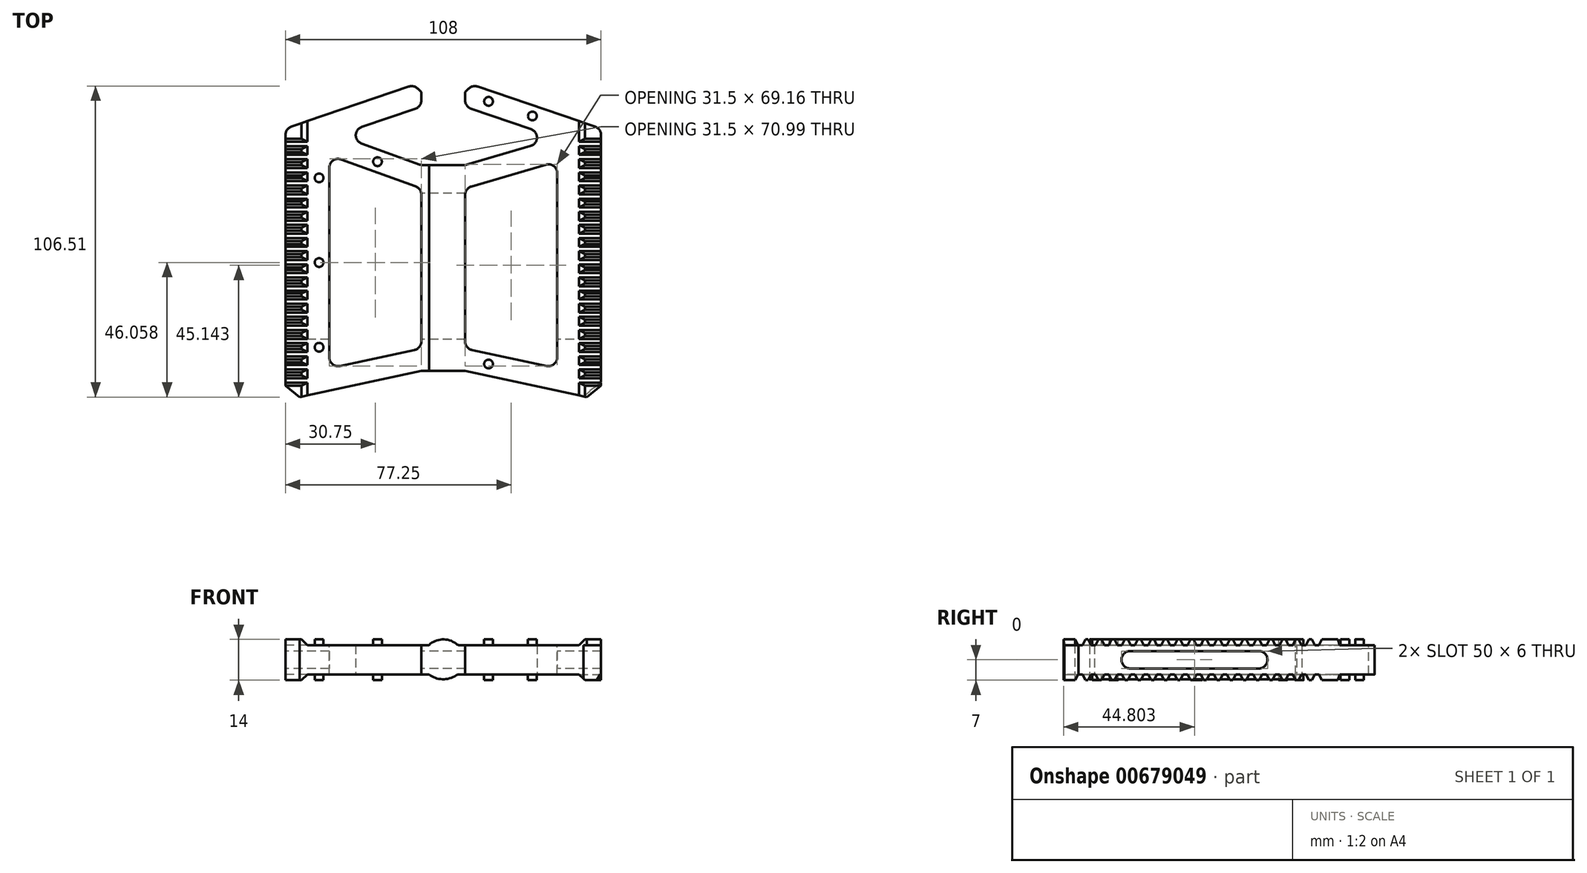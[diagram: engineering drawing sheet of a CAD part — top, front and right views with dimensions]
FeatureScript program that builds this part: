
annotation { "Feature Type Name" : "Feature", "Feature Type Description" : "" }
export const myFeature = defineFeature(function(context is Context, id is Id, definition is map)
    precondition{}
    {
        {
            var Q0;
            Q0=qCreatedBy(makeId("Top.planeOp"),FACE);
            var sketch = newSketch(context, id + "F0", { "sketchPlane" : qUnion([Q0])});
            skLineSegment(sketch, "E0.top", {"start": v(44, 108) * mm, "end": v(64, 108) * mm});
            skLineSegment(sketch, "E0.left", {"start": v(0, 0) * mm, "end": v(0, 93) * mm});
            skLineSegment(sketch, "E0.right", {"start": v(108, 0) * mm, "end": v(108, 93) * mm});
            skLineSegment(sketch, "E1", {"start": v(0, 0) * mm, "end": v(46.5, 10) * mm});
            skLineSegment(sketch, "E2", {"start": v(46.5, 10) * mm, "end": v(61.5, 10) * mm});
            skLineSegment(sketch, "E3", {"start": v(61.5, 10) * mm, "end": v(108, 0) * mm});
            skLineSegment(sketch, "E4", {"start": v(0, 93) * mm, "end": v(44, 108) * mm});
            skLineSegment(sketch, "E5", {"start": v(64, 108) * mm, "end": v(108, 93) * mm});
            skPoint(sketch, "E6.orphan", {"position": v(0, 108) * mm});
            skSolve(sketch);
        }
        {
            var Q0;
            Q0=qSketchRegion(id+"F0",true);
            extrude(context, id + "F1", {"entities" : qUnion([Q0]), "depth" : 10 * mm, "offsetDistance" : 25 * mm});
        }
        {
            var Q0;
            Q0=makeQuery(id+"F1.opExtrude","CAP_FACE",FACE,{"disambiguationData":[OSD([sQuery(id+"F0.wireOp",EDGE,"E0.top"),sQuery(id+"F0.wireOp",EDGE,"E0.left"),sQuery(id+"F0.wireOp",EDGE,"E0.right"),sQuery(id+"F0.wireOp",EDGE,"E1"),sQuery(id+"F0.wireOp",EDGE,"E2"),sQuery(id+"F0.wireOp",EDGE,"E3"),sQuery(id+"F0.wireOp",EDGE,"E4"),sQuery(id+"F0.wireOp",EDGE,"E5")])],"isStart":false});
            var sketch = newSketch(context, id + "F2", { "sketchPlane" : qUnion([Q0])});
            skLineSegment(sketch, "E7", {"start": v(18, 90.78) * mm, "end": v(46.5, 100.5) * mm});
            skLineSegment(sketch, "E8", {"start": v(61.5, 100.5) * mm, "end": v(93, 89.76) * mm});
            skLineSegment(sketch, "E9", {"start": v(93, 89.76) * mm, "end": v(61.5, 80.5) * mm});
            skLineSegment(sketch, "E10", {"start": v(61.5, 80.5) * mm, "end": v(46.5, 80.5) * mm});
            skLineSegment(sketch, "E11", {"start": v(46.5, 80.5) * mm, "end": v(18, 90.78) * mm});
            skLineSegment(sketch, "E12", {"start": v(15, 83.9) * mm, "end": v(46.5, 72.53) * mm});
            skLineSegment(sketch, "E13", {"start": v(46.5, 72.53) * mm, "end": v(46.5, 17.67) * mm});
            skLineSegment(sketch, "E14", {"start": v(46.5, 17.67) * mm, "end": v(15, 10.9) * mm});
            skLineSegment(sketch, "E15", {"start": v(15, 10.9) * mm, "end": v(15, 83.9) * mm});
            skLineSegment(sketch, "E16", {"start": v(61.5, 72.53) * mm, "end": v(93, 81.79) * mm});
            skLineSegment(sketch, "E17", {"start": v(93, 81.79) * mm, "end": v(93, 10.9) * mm});
            skLineSegment(sketch, "E18", {"start": v(93, 10.9) * mm, "end": v(61.5, 17.67) * mm});
            skLineSegment(sketch, "E19", {"start": v(61.5, 17.67) * mm, "end": v(61.5, 72.53) * mm});
            skLineSegment(sketch, "E20", {"start": v(44, 108) * mm, "end": v(46.5, 105.5) * mm});
            skLineSegment(sketch, "E21", {"start": v(61.5, 105.5) * mm, "end": v(64, 108) * mm});
            skLineSegment(sketch, "E22", {"start": v(46.5, 105.5) * mm, "end": v(46.5, 100.5) * mm});
            skLineSegment(sketch, "E23", {"start": v(61.5, 105.5) * mm, "end": v(61.5, 100.5) * mm});
            skSolve(sketch);
        }
        {
            var Q0;
            Q0=makeQuery(id+"F2.imprint","IMPRINT",FACE,{"disambiguationData":[TD([[makeQuery(id+"F2.imprint","IMPRINT",EDGE,{"derivedFrom":sQuery(id+"F2.wireOp",EDGE,"E12")}),-1.0]])]});
            var Q1;
            Q1=makeQuery(id+"F2.imprint","IMPRINT",FACE,{"disambiguationData":[TD([[makeQuery(id+"F2.imprint","IMPRINT",EDGE,{"derivedFrom":sQuery(id+"F2.wireOp",EDGE,"E16")}),-1.0]])]});
            var Q2;
            Q2=makeQuery(id+"F2.imprint","IMPRINT",FACE,{"disambiguationData":[TD([[makeQuery(id+"F2.imprint","IMPRINT",EDGE,{"derivedFrom":sQuery(id+"F2.wireOp",EDGE,"E7")}),-1.0]])]});
            var Q3;
            Q3=makeQuery(id+"F2.imprint","IMPRINT",FACE,{"disambiguationData":[TD([[makeQuery(id+"F2.imprint","IMPRINT",EDGE,{"derivedFrom":sQuery(id+"F2.wireOp",EDGE,"E20")}),1.0]])]});
            extrude(context, id + "F3", {"entities" : qUnion([Q0, Q1, Q2, Q3]), "operationType" : NewBodyOperationType.REMOVE, "oppositeDirection" : true, "depth" : 25 * mm, "offsetDistance" : 25 * mm});
        }
        {
            var Q0;
            Q0=makeQuery(id+"F1.opExtrude","SWEPT_EDGE",EDGE,{"disambiguationData":[OSD([sQuery(id+"F0.wireOp",EDGE,"E0.left"),sQuery(id+"F0.wireOp",EDGE,"E1")])]});
            var Q1;
            Q1=makeQuery(id+"F1.opExtrude","SWEPT_EDGE",EDGE,{"disambiguationData":[OSD([sQuery(id+"F0.wireOp",EDGE,"E0.right"),sQuery(id+"F0.wireOp",EDGE,"E3")])]});
            chamfer(context, id + "F4", {"entities" : qUnion([Q0, Q1]), "width" : 5 * mm, "tangentPropagation" : true});
        }
        {
            var Q0;
            Q0=makeQuery(id+"F3.boolean.opBoolean","COPY",EDGE,{"derivedFrom":makeQuery(id+"F3.opExtrude","SWEPT_EDGE",EDGE,{"disambiguationData":[OSD([sQuery(id+"F2.wireOp",EDGE,"E13"),sQuery(id+"F2.wireOp",EDGE,"E14")])]})});
            var Q1;
            Q1=makeQuery(id+"F3.boolean.opBoolean","COPY",EDGE,{"derivedFrom":makeQuery(id+"F3.opExtrude","SWEPT_EDGE",EDGE,{"disambiguationData":[OSD([sQuery(id+"F2.wireOp",EDGE,"E17"),sQuery(id+"F2.wireOp",EDGE,"E18")])]})});
            var Q2;
            Q2=makeQuery(id+"F3.boolean.opBoolean","COPY",EDGE,{"derivedFrom":makeQuery(id+"F3.opExtrude","SWEPT_EDGE",EDGE,{"disambiguationData":[OSD([sQuery(id+"F2.wireOp",EDGE,"E10"),sQuery(id+"F2.wireOp",EDGE,"E11")])]})});
            var Q3;
            Q3=makeQuery(id+"F3.boolean.opBoolean","COPY",EDGE,{"derivedFrom":makeQuery(id+"F3.opExtrude","SWEPT_EDGE",EDGE,{"disambiguationData":[OSD([sQuery(id+"F2.wireOp",EDGE,"E9"),sQuery(id+"F2.wireOp",EDGE,"E10")])]})});
            var Q4;
            Q4=makeQuery(id+"F3.boolean.opBoolean","COPY",EDGE,{"derivedFrom":makeQuery(id+"F3.opExtrude","SWEPT_EDGE",EDGE,{"disambiguationData":[OSD([sQuery(id+"F2.wireOp",EDGE,"E18"),sQuery(id+"F2.wireOp",EDGE,"E19")])]})});
            var Q5;
            Q5=makeQuery(id+"F3.boolean.opBoolean","COPY",EDGE,{"derivedFrom":makeQuery(id+"F3.opExtrude","SWEPT_EDGE",EDGE,{"disambiguationData":[OSD([sQuery(id+"F2.wireOp",EDGE,"E14"),sQuery(id+"F2.wireOp",EDGE,"E15")])]})});
            var Q6;
            Q6=makeQuery(id+"F3.boolean.opBoolean","COPY",EDGE,{"derivedFrom":makeQuery(id+"F3.opExtrude","SWEPT_EDGE",EDGE,{"disambiguationData":[OSD([sQuery(id+"F2.wireOp",EDGE,"E16"),sQuery(id+"F2.wireOp",EDGE,"E17")])]})});
            var Q7;
            Q7=makeQuery(id+"F3.boolean.opBoolean","COPY",EDGE,{"derivedFrom":makeQuery(id+"F3.opExtrude","SWEPT_EDGE",EDGE,{"disambiguationData":[OSD([sQuery(id+"F2.wireOp",EDGE,"E12"),sQuery(id+"F2.wireOp",EDGE,"E13")])]})});
            var Q8;
            Q8=makeQuery(id+"F3.boolean.opBoolean","COPY",EDGE,{"derivedFrom":makeQuery(id+"F3.opExtrude","SWEPT_EDGE",EDGE,{"disambiguationData":[OSD([sQuery(id+"F2.wireOp",EDGE,"E12"),sQuery(id+"F2.wireOp",EDGE,"E15")])]})});
            var Q9;
            Q9=makeQuery(id+"F3.boolean.opBoolean","COPY",EDGE,{"derivedFrom":makeQuery(id+"F3.opExtrude","SWEPT_EDGE",EDGE,{"disambiguationData":[OSD([sQuery(id+"F2.wireOp",EDGE,"E7"),sQuery(id+"F2.wireOp",EDGE,"HO8CVhf7-1jhG-dmqV-wMaq-zJcC65SmTLqd")])]})});
            var Q10;
            Q10=makeQuery(id+"F3.boolean.opBoolean","COPY",EDGE,{"derivedFrom":makeQuery(id+"F3.opExtrude","SWEPT_EDGE",EDGE,{"disambiguationData":[OSD([sQuery(id+"F2.wireOp",EDGE,"HO8CVhf7-1jhG-dmqV-wMaq-zJcC65SmTLqd"),sQuery(id+"F2.wireOp",EDGE,"E8")])]})});
            var Q11;
            Q11=makeQuery(id+"F3.boolean.opBoolean","COPY",EDGE,{"derivedFrom":makeQuery(id+"F3.opExtrude","SWEPT_EDGE",EDGE,{"disambiguationData":[OSD([sQuery(id+"F2.wireOp",EDGE,"E8"),sQuery(id+"F2.wireOp",EDGE,"E9")])]})});
            var Q12;
            Q12=makeQuery(id+"F3.boolean.opBoolean","COPY",EDGE,{"derivedFrom":makeQuery(id+"F3.opExtrude","SWEPT_EDGE",EDGE,{"disambiguationData":[OSD([sQuery(id+"F2.wireOp",EDGE,"E7"),sQuery(id+"F2.wireOp",EDGE,"E11")])]})});
            var Q13;
            Q13=makeQuery(id+"F3.boolean.opBoolean","COPY",EDGE,{"derivedFrom":makeQuery(id+"F3.opExtrude","SWEPT_EDGE",EDGE,{"disambiguationData":[OSD([sQuery(id+"F2.wireOp",EDGE,"E16"),sQuery(id+"F2.wireOp",EDGE,"E19")])]})});
            var Q14;
            Q14=makeQuery(id+"F1.opExtrude","SWEPT_EDGE",EDGE,{"disambiguationData":[OSD([sQuery(id+"F0.wireOp",EDGE,"E0.right"),sQuery(id+"F0.wireOp",EDGE,"E5")])]});
            var Q15;
            Q15=makeQuery(id+"F1.opExtrude","SWEPT_EDGE",EDGE,{"disambiguationData":[OSD([sQuery(id+"F0.wireOp",EDGE,"E0.left"),sQuery(id+"F0.wireOp",EDGE,"E4")])]});
            var Q16;
            {var subQ0=sQuery(id+"F0.wireOp",EDGE,"E5");var subQ1=sQuery(id+"F0.wireOp",EDGE,"E0.top");Q16=makeQuery(id+"F3.boolean.opBoolean","MERGE",EDGE,{"derivedFrom":[makeQuery(id+"F1.opExtrude","SWEPT_EDGE",EDGE,{"disambiguationData":[OSD([subQ1,subQ0])]}),makeQuery(id+"F3.opExtrude","SWEPT_EDGE",EDGE,{"disambiguationData":[OSD([subQ1,subQ0,sQuery(id+"F2.wireOp",EDGE,"E21")])]})]});}
            var Q17;
            {var subQ0=sQuery(id+"F0.wireOp",EDGE,"E4");var subQ1=sQuery(id+"F0.wireOp",EDGE,"E0.top");Q17=makeQuery(id+"F3.boolean.opBoolean","MERGE",EDGE,{"derivedFrom":[makeQuery(id+"F1.opExtrude","SWEPT_EDGE",EDGE,{"disambiguationData":[OSD([subQ1,subQ0])]}),makeQuery(id+"F3.opExtrude","SWEPT_EDGE",EDGE,{"disambiguationData":[OSD([subQ1,subQ0,sQuery(id+"F2.wireOp",EDGE,"E20")])]})]});}
            fillet(context, id + "F5", {"entities" : qUnion([Q0, Q1, Q2, Q3, Q4, Q5, Q6, Q7, Q8, Q9, Q10, Q11, Q12, Q13, Q14, Q15, Q16, Q17]), "radius" : 3 * mm, "tangentPropagation" : true, "allowEdgeOverflow" : false});
        }
        {
            var Q0;
            Q0=makeQuery(id+"F1.opExtrude","CAP_FACE",FACE,{"disambiguationData":[OSD([sQuery(id+"F0.wireOp",EDGE,"E0.top"),sQuery(id+"F0.wireOp",EDGE,"E0.left"),sQuery(id+"F0.wireOp",EDGE,"E0.right"),sQuery(id+"F0.wireOp",EDGE,"E1"),sQuery(id+"F0.wireOp",EDGE,"E2"),sQuery(id+"F0.wireOp",EDGE,"E3"),sQuery(id+"F0.wireOp",EDGE,"E4"),sQuery(id+"F0.wireOp",EDGE,"E5")])],"isStart":false});
            var sketch = newSketch(context, id + "F6", { "sketchPlane" : qUnion([Q0])});
            skLineSegment(sketch, "E24", {"start": v(100.5, 95.56) * mm, "end": v(100.5, 1.61) * mm});
            skLineSegment(sketch, "E25", {"start": v(103.11, 1.05) * mm, "end": v(108, 5) * mm});
            skLineSegment(sketch, "E26", {"start": v(108, 5) * mm, "end": v(108, 90.85) * mm});
            skLineSegment(sketch, "E27", {"start": v(100.5, 95.56) * mm, "end": v(105.97, 93.7) * mm});
            skArc(sketch, "E28", {"start": v(108, 90.85) * mm, "mid": v(107.44, 92.6) * mm, "end": v(105.97, 93.7) * mm});
            skLineSegment(sketch, "E29", {"start": v(103.11, 1.05) * mm, "end": v(100.5, 1.61) * mm});
            skSolve(sketch);
        }
        {
            var Q0;
            {var subQ2=sQuery(id+"F6.wireOp",EDGE,"E24");Q0=makeQuery(id+"F6.imprint","IMPRINT",FACE,{"disambiguationData":[TD([[makeQuery(id+"F6.imprint","IMPRINT",EDGE,{"derivedFrom":subQ2}),1.0]])]});}
            extrude(context, id + "F7", {"entities" : qUnion([Q0]), "operationType" : NewBodyOperationType.ADD, "depth" : 2 * mm, "offsetDistance" : 25 * mm, "hasSecondDirection" : true, "secondDirectionOppositeDirection" : true, "secondDirectionDepth" : 12 * mm});
        }
        {
            var Q0;
            Q0=qSketchRegion(id+"F6",true);
            extrude(context, id + "F8", {"entities" : qUnion([Q0]), "operationType" : NewBodyOperationType.ADD, "depth" : 2 * mm, "offsetDistance" : 25 * mm});
        }
        {
            var Q0;
            Q0=makeQuery(id+"F1.opExtrude","CAP_FACE",FACE,{"disambiguationData":[OSD([sQuery(id+"F0.wireOp",EDGE,"E0.top"),sQuery(id+"F0.wireOp",EDGE,"E0.left"),sQuery(id+"F0.wireOp",EDGE,"E0.right"),sQuery(id+"F0.wireOp",EDGE,"E1"),sQuery(id+"F0.wireOp",EDGE,"E2"),sQuery(id+"F0.wireOp",EDGE,"E3"),sQuery(id+"F0.wireOp",EDGE,"E4"),sQuery(id+"F0.wireOp",EDGE,"E5")])],"isStart":true});
            var sketch = newSketch(context, id + "F9", { "sketchPlane" : qUnion([Q0])});
            skLineSegment(sketch, "E30", {"start": v(7.5, -95.56) * mm, "end": v(7.5, -1.61) * mm});
            skLineSegment(sketch, "E31", {"start": v(7.5, -1.61) * mm, "end": v(4.89, -1.05) * mm});
            skLineSegment(sketch, "E32", {"start": v(4.89, -1.05) * mm, "end": v(0, -5) * mm});
            skLineSegment(sketch, "E33", {"start": v(0, -5) * mm, "end": v(0, -90.85) * mm});
            skLineSegment(sketch, "E34", {"start": v(2.03, -93.7) * mm, "end": v(7.5, -95.56) * mm});
            skArc(sketch, "E35", {"start": v(0, -90.85) * mm, "mid": v(0.56, -92.6) * mm, "end": v(2.03, -93.7) * mm});
            skSolve(sketch);
        }
        {
            var Q0;
            Q0=qSketchRegion(id+"F9",true);
            extrude(context, id + "F10", {"entities" : qUnion([Q0]), "operationType" : NewBodyOperationType.ADD, "depth" : 2 * mm, "offsetDistance" : 25 * mm, "hasSecondDirection" : true, "secondDirectionOppositeDirection" : true, "secondDirectionDepth" : 12 * mm});
        }
        {
            var Q0;
            Q0=makeQuery(id+"F7.opExtrude","CAP_EDGE",EDGE,{"disambiguationData":[OSD([sQuery(id+"F6.wireOp",EDGE,"E24")])],"isStart":false});
            var Q1;
            Q1=makeQuery(id+"F10.opExtrude","CAP_EDGE",EDGE,{"disambiguationData":[OSD([sQuery(id+"F9.wireOp",EDGE,"E30")])],"isStart":false});
            var Q2;
            Q2=makeQuery(id+"F7.opExtrude","CAP_EDGE",EDGE,{"disambiguationData":[OSD([sQuery(id+"F6.wireOp",EDGE,"E24")])],"isStart":true});
            var Q3;
            Q3=makeQuery(id+"F10.opExtrude","CAP_EDGE",EDGE,{"disambiguationData":[OSD([sQuery(id+"F9.wireOp",EDGE,"E30")])],"isStart":true});
            chamfer(context, id + "F11", {"entities" : qUnion([Q0, Q1, Q2, Q3]), "width" : 2 * mm, "tangentPropagation" : true});
        }
        {
            var Q0;
            Q0=makeQuery(id+"F1.opExtrude","CAP_FACE",FACE,{"disambiguationData":[OSD([sQuery(id+"F0.wireOp",EDGE,"E0.top"),sQuery(id+"F0.wireOp",EDGE,"E0.left"),sQuery(id+"F0.wireOp",EDGE,"E0.right"),sQuery(id+"F0.wireOp",EDGE,"E1"),sQuery(id+"F0.wireOp",EDGE,"E2"),sQuery(id+"F0.wireOp",EDGE,"E3"),sQuery(id+"F0.wireOp",EDGE,"E4"),sQuery(id+"F0.wireOp",EDGE,"E5")])],"isStart":false});
            var sketch = newSketch(context, id + "F12", { "sketchPlane" : qUnion([Q0])});
            skCircle(sketch, "E36", {"center": v(69.5, 102.34) * mm, "radius": 1.5 * mm});
            skCircle(sketch, "E37", {"center": v(84.5, 97.31) * mm, "radius": 1.5 * mm});
            skCircle(sketch, "E38", {"center": v(69.5, 12.37) * mm, "radius": 1.5 * mm});
            skCircle(sketch, "E39", {"center": v(11.5, 76.12) * mm, "radius": 1.5 * mm});
            skCircle(sketch, "E40", {"center": v(11.5, 47.12) * mm, "radius": 1.5 * mm});
            skCircle(sketch, "E41", {"center": v(11.5, 18.11) * mm, "radius": 1.5 * mm});
            skCircle(sketch, "E42", {"center": v(31.5, 81.66) * mm, "radius": 1.5 * mm});
            skSolve(sketch);
        }
        {
            var Q0;
            Q0=qSketchRegion(id+"F12",true);
            extrude(context, id + "F13", {"entities" : qUnion([Q0]), "operationType" : NewBodyOperationType.ADD, "depth" : 2 * mm, "offsetDistance" : 25 * mm, "hasSecondDirection" : true, "secondDirectionOppositeDirection" : true, "secondDirectionDepth" : 12 * mm});
        }
        {
            var Q0;
            Q0=makeQuery(id+"F1.opExtrude","SWEPT_FACE",FACE,{"disambiguationData":[OSD([sQuery(id+"F0.wireOp",EDGE,"E2")])]});
            var sketch = newSketch(context, id + "F14", { "sketchPlane" : qUnion([Q0])});
            skArc(sketch, "E43", {"start": v(58.9, 10) * mm, "mid": v(54, 12) * mm, "end": v(49.1, 10) * mm});
            skArc(sketch, "E44", {"start": v(49.1, 0) * mm, "mid": v(54, -1.68) * mm, "end": v(58.9, 0) * mm});
            skLineSegment(sketch, "E45", {"start": v(49.1, 10) * mm, "end": v(58.9, 10) * mm});
            skLineSegment(sketch, "E46", {"start": v(58.9, 0) * mm, "end": v(49.1, 0) * mm});
            skSolve(sketch);
        }
        {
            var Q0;
            Q0=makeQuery(id+"F14.imprint","IMPRINT",FACE,{"disambiguationData":[TD([[makeQuery(id+"F14.imprint","IMPRINT",EDGE,{"derivedFrom":sQuery(id+"F14.wireOp",EDGE,"E43")}),1.0]])]});
            var Q1;
            Q1=makeQuery(id+"F14.imprint","IMPRINT",FACE,{"disambiguationData":[TD([[makeQuery(id+"F14.imprint","IMPRINT",EDGE,{"derivedFrom":sQuery(id+"F14.wireOp",EDGE,"E44")}),1.0]])]});
            var Q2;
            Q2=makeQuery(id+"F3.boolean.opBoolean","COPY",FACE,{"derivedFrom":makeQuery(id+"F3.opExtrude","SWEPT_FACE",FACE,{"disambiguationData":[OSD([sQuery(id+"F2.wireOp",EDGE,"E10")])]})});
            extrude(context, id + "F15", {"entities" : qUnion([Q0, Q1]), "operationType" : NewBodyOperationType.ADD, "endBound" : BoundingType.UP_TO_SURFACE, "oppositeDirection" : true, "depth" : 25 * mm, "endBoundEntityFace" : qUnion([Q2]), "offsetDistance" : 25 * mm});
        }
        {
            var Q0;
            {var subQ0=sQuery(id+"F14.wireOp",EDGE,"E46");var subQ1=sQuery(id+"F14.wireOp",EDGE,"E44");var subQ2=sQuery(id+"F0.wireOp",EDGE,"E2");Q0=makeQuery(id+"F15.opExtrude","SWEPT_EDGE",EDGE,{"disambiguationData":[OSD([subQ2,subQ1,subQ0]),TDD([makeQuery(id+"F14.imprint","INTERSECT",VERTEX,{"disambiguationData":[OD(0.0)],"derivedFrom":[makeQuery(id+"F1.opExtrude","CAP_EDGE",EDGE,{"disambiguationData":[OSD([subQ2])],"isStart":true}),subQ1,subQ0]})])]});}
            var Q1;
            {var subQ0=sQuery(id+"F14.wireOp",EDGE,"E46");var subQ1=sQuery(id+"F14.wireOp",EDGE,"E44");var subQ2=sQuery(id+"F0.wireOp",EDGE,"E2");Q1=makeQuery(id+"F15.opExtrude","SWEPT_EDGE",EDGE,{"disambiguationData":[OSD([subQ2,subQ1,subQ0]),TDD([makeQuery(id+"F14.imprint","INTERSECT",VERTEX,{"disambiguationData":[OD(1.0)],"derivedFrom":[makeQuery(id+"F1.opExtrude","CAP_EDGE",EDGE,{"disambiguationData":[OSD([subQ2])],"isStart":true}),subQ1,subQ0]})])]});}
            var Q2;
            {var subQ0=sQuery(id+"F14.wireOp",EDGE,"E45");var subQ1=sQuery(id+"F14.wireOp",EDGE,"E43");var subQ2=sQuery(id+"F0.wireOp",EDGE,"E2");Q2=makeQuery(id+"F15.opExtrude","SWEPT_EDGE",EDGE,{"disambiguationData":[OSD([subQ2,subQ1,subQ0]),TDD([makeQuery(id+"F14.imprint","INTERSECT",VERTEX,{"disambiguationData":[OD(1.0)],"derivedFrom":[makeQuery(id+"F1.opExtrude","CAP_EDGE",EDGE,{"disambiguationData":[OSD([subQ2])],"isStart":false}),subQ1,subQ0]})])]});}
            var Q3;
            {var subQ0=sQuery(id+"F14.wireOp",EDGE,"E45");var subQ1=sQuery(id+"F14.wireOp",EDGE,"E43");var subQ2=sQuery(id+"F0.wireOp",EDGE,"E2");Q3=makeQuery(id+"F15.opExtrude","SWEPT_EDGE",EDGE,{"disambiguationData":[OSD([subQ2,subQ1,subQ0]),TDD([makeQuery(id+"F14.imprint","INTERSECT",VERTEX,{"disambiguationData":[OD(0.0)],"derivedFrom":[makeQuery(id+"F1.opExtrude","CAP_EDGE",EDGE,{"disambiguationData":[OSD([subQ2])],"isStart":false}),subQ1,subQ0]})])]});}
            fillet(context, id + "F16", {"entities" : qUnion([Q0, Q1, Q2, Q3]), "radius" : 2 * mm, "tangentPropagation" : true, "allowEdgeOverflow" : false});
        }
        {
            var Q0;
            Q0=makeQuery(id+"F10.boolean.opBoolean","MERGE",FACE,{"derivedFrom":[makeQuery(id+"F1.opExtrude","SWEPT_FACE",FACE,{"disambiguationData":[OSD([sQuery(id+"F0.wireOp",EDGE,"E0.left")])]}),makeQuery(id+"F10.opExtrude","SWEPT_FACE",FACE,{"disambiguationData":[OSD([sQuery(id+"F9.wireOp",EDGE,"E33")])]})]});
            cPlane(context, id + "F17", {"entities" : qUnion([Q0]), "cplaneType" : CPlaneType.OFFSET, "offset" : 54 * mm, "oppositeDirection" : true, "width" : 150 * mm, "height" : 150 * mm});
        }
        {
            var Q0;
            Q0=qCreatedBy(id+"F17.planeOp",FACE);
            var sketch = newSketch(context, id + "F18", { "sketchPlane" : qUnion([Q0])});
            skLineSegment(sketch, "E47.bottom", {"start": v(-67.85, 8) * mm, "end": v(-23.85, 8) * mm});
            skLineSegment(sketch, "E47.top", {"start": v(-67.85, 2) * mm, "end": v(-23.85, 2) * mm});
            skLineSegment(sketch, "E47.left", {"start": v(-70.85, 5) * mm, "end": v(-70.85, 5) * mm});
            skLineSegment(sketch, "E47.right", {"start": v(-20.85, 5) * mm, "end": v(-20.85, 5) * mm});
            skPoint(sketch, "E48.visualSharp", {"position": v(-70.85, 8) * mm});
            skArc(sketch, "E48.filletArc", {"start": v(-67.85, 8) * mm, "mid": v(-69.97, 7.12) * mm, "end": v(-70.85, 5) * mm});
            skPoint(sketch, "E49.visualSharp", {"position": v(-70.85, 2) * mm});
            skArc(sketch, "E49.filletArc", {"start": v(-70.85, 5) * mm, "mid": v(-69.97, 2.88) * mm, "end": v(-67.85, 2) * mm});
            skPoint(sketch, "E50.visualSharp", {"position": v(-20.85, 2) * mm});
            skArc(sketch, "E50.filletArc", {"start": v(-23.85, 2) * mm, "mid": v(-21.73, 2.88) * mm, "end": v(-20.85, 5) * mm});
            skPoint(sketch, "E51.visualSharp", {"position": v(-20.85, 8) * mm});
            skArc(sketch, "E51.filletArc", {"start": v(-20.85, 5) * mm, "mid": v(-21.73, 7.12) * mm, "end": v(-23.85, 8) * mm});
            skSolve(sketch);
        }
        {
            var Q0;
            Q0 = qSketchRegion(id + "F18", true);
            extrude(context, id + "F19", {"entities" : qUnion([Q0]), "operationType" : NewBodyOperationType.REMOVE, "endBound" : BoundingType.THROUGH_ALL, "oppositeDirection" : true, "depth" : 25 * mm, "offsetDistance" : 25 * mm, "hasSecondDirection" : true, "secondDirectionBound" : SecondDirectionBoundingType.THROUGH_ALL, "secondDirectionOppositeDirection" : false, "secondDirectionDepth" : 25 * mm});
        }
        {
            var Q0;
            Q0=makeQuery(id+"F10.boolean.opBoolean","MERGE",FACE,{"derivedFrom":[makeQuery(id+"F1.opExtrude","SWEPT_FACE",FACE,{"disambiguationData":[OSD([sQuery(id+"F0.wireOp",EDGE,"E0.left")])]}),makeQuery(id+"F10.opExtrude","SWEPT_FACE",FACE,{"disambiguationData":[OSD([sQuery(id+"F9.wireOp",EDGE,"E33")])]})]});
            var sketch = newSketch(context, id + "F20", { "sketchPlane" : qUnion([Q0])});
            skLineSegment(sketch, "E52", {"start": v(-5, 12) * mm, "end": v(-6, 10) * mm});
            skLineSegment(sketch, "E53", {"start": v(-6, 10) * mm, "end": v(-7.5, 10) * mm});
            skLineSegment(sketch, "E54", {"start": v(-7.5, 10) * mm, "end": v(-8.5, 12) * mm});
            skLineSegment(sketch, "E55", {"start": v(-8.5, 12) * mm, "end": v(-5, 12) * mm});
            skLineSegment(sketch, "E56.1.0.0", {"start": v(-9.5, 12) * mm, "end": v(-10.5, 10) * mm});
            skLineSegment(sketch, "E56.1.0.1", {"start": v(-10.5, 10) * mm, "end": v(-12, 10) * mm});
            skLineSegment(sketch, "E56.1.0.2", {"start": v(-12, 10) * mm, "end": v(-13, 12) * mm});
            skLineSegment(sketch, "E56.1.0.3", {"start": v(-13, 12) * mm, "end": v(-9.5, 12) * mm});
            skLineSegment(sketch, "E56.2.0.0", {"start": v(-14, 12) * mm, "end": v(-15, 10) * mm});
            skLineSegment(sketch, "E56.2.0.1", {"start": v(-15, 10) * mm, "end": v(-16.5, 10) * mm});
            skLineSegment(sketch, "E56.2.0.2", {"start": v(-16.5, 10) * mm, "end": v(-17.5, 12) * mm});
            skLineSegment(sketch, "E56.2.0.3", {"start": v(-17.5, 12) * mm, "end": v(-14, 12) * mm});
            skLineSegment(sketch, "E56.3.0.0", {"start": v(-18.5, 12) * mm, "end": v(-19.5, 10) * mm});
            skLineSegment(sketch, "E56.3.0.1", {"start": v(-19.5, 10) * mm, "end": v(-21, 10) * mm});
            skLineSegment(sketch, "E56.3.0.2", {"start": v(-21, 10) * mm, "end": v(-22, 12) * mm});
            skLineSegment(sketch, "E56.3.0.3", {"start": v(-22, 12) * mm, "end": v(-18.5, 12) * mm});
            skLineSegment(sketch, "E56.4.0.0", {"start": v(-23, 12) * mm, "end": v(-24, 10) * mm});
            skLineSegment(sketch, "E56.4.0.1", {"start": v(-24, 10) * mm, "end": v(-25.5, 10) * mm});
            skLineSegment(sketch, "E56.4.0.2", {"start": v(-25.5, 10) * mm, "end": v(-26.5, 12) * mm});
            skLineSegment(sketch, "E56.4.0.3", {"start": v(-26.5, 12) * mm, "end": v(-23, 12) * mm});
            skLineSegment(sketch, "E56.5.0.0", {"start": v(-27.5, 12) * mm, "end": v(-28.5, 10) * mm});
            skLineSegment(sketch, "E56.5.0.1", {"start": v(-28.5, 10) * mm, "end": v(-30, 10) * mm});
            skLineSegment(sketch, "E56.5.0.2", {"start": v(-30, 10) * mm, "end": v(-31, 12) * mm});
            skLineSegment(sketch, "E56.5.0.3", {"start": v(-31, 12) * mm, "end": v(-27.5, 12) * mm});
            skLineSegment(sketch, "E56.6.0.0", {"start": v(-32, 12) * mm, "end": v(-33, 10) * mm});
            skLineSegment(sketch, "E56.6.0.1", {"start": v(-33, 10) * mm, "end": v(-34.5, 10) * mm});
            skLineSegment(sketch, "E56.6.0.2", {"start": v(-34.5, 10) * mm, "end": v(-35.5, 12) * mm});
            skLineSegment(sketch, "E56.6.0.3", {"start": v(-35.5, 12) * mm, "end": v(-32, 12) * mm});
            skLineSegment(sketch, "E56.7.0.0", {"start": v(-36.5, 12) * mm, "end": v(-37.5, 10) * mm});
            skLineSegment(sketch, "E56.7.0.1", {"start": v(-37.5, 10) * mm, "end": v(-39, 10) * mm});
            skLineSegment(sketch, "E56.7.0.2", {"start": v(-39, 10) * mm, "end": v(-40, 12) * mm});
            skLineSegment(sketch, "E56.7.0.3", {"start": v(-40, 12) * mm, "end": v(-36.5, 12) * mm});
            skLineSegment(sketch, "E56.8.0.0", {"start": v(-41, 12) * mm, "end": v(-42, 10) * mm});
            skLineSegment(sketch, "E56.8.0.1", {"start": v(-42, 10) * mm, "end": v(-43.5, 10) * mm});
            skLineSegment(sketch, "E56.8.0.2", {"start": v(-43.5, 10) * mm, "end": v(-44.5, 12) * mm});
            skLineSegment(sketch, "E56.8.0.3", {"start": v(-44.5, 12) * mm, "end": v(-41, 12) * mm});
            skLineSegment(sketch, "E56.9.0.0", {"start": v(-45.5, 12) * mm, "end": v(-46.5, 10) * mm});
            skLineSegment(sketch, "E56.9.0.1", {"start": v(-46.5, 10) * mm, "end": v(-48, 10) * mm});
            skLineSegment(sketch, "E56.9.0.2", {"start": v(-48, 10) * mm, "end": v(-49, 12) * mm});
            skLineSegment(sketch, "E56.9.0.3", {"start": v(-49, 12) * mm, "end": v(-45.5, 12) * mm});
            skLineSegment(sketch, "E56.10.0.0", {"start": v(-50, 12) * mm, "end": v(-51, 10) * mm});
            skLineSegment(sketch, "E56.10.0.1", {"start": v(-51, 10) * mm, "end": v(-52.5, 10) * mm});
            skLineSegment(sketch, "E56.10.0.2", {"start": v(-52.5, 10) * mm, "end": v(-53.5, 12) * mm});
            skLineSegment(sketch, "E56.10.0.3", {"start": v(-53.5, 12) * mm, "end": v(-50, 12) * mm});
            skLineSegment(sketch, "E56.11.0.0", {"start": v(-54.5, 12) * mm, "end": v(-55.5, 10) * mm});
            skLineSegment(sketch, "E56.11.0.1", {"start": v(-55.5, 10) * mm, "end": v(-57, 10) * mm});
            skLineSegment(sketch, "E56.11.0.2", {"start": v(-57, 10) * mm, "end": v(-58, 12) * mm});
            skLineSegment(sketch, "E56.11.0.3", {"start": v(-58, 12) * mm, "end": v(-54.5, 12) * mm});
            skLineSegment(sketch, "E56.12.0.0", {"start": v(-59, 12) * mm, "end": v(-60, 10) * mm});
            skLineSegment(sketch, "E56.12.0.1", {"start": v(-60, 10) * mm, "end": v(-61.5, 10) * mm});
            skLineSegment(sketch, "E56.12.0.2", {"start": v(-61.5, 10) * mm, "end": v(-62.5, 12) * mm});
            skLineSegment(sketch, "E56.12.0.3", {"start": v(-62.5, 12) * mm, "end": v(-59, 12) * mm});
            skLineSegment(sketch, "E56.13.0.0", {"start": v(-63.5, 12) * mm, "end": v(-64.5, 10) * mm});
            skLineSegment(sketch, "E56.13.0.1", {"start": v(-64.5, 10) * mm, "end": v(-66, 10) * mm});
            skLineSegment(sketch, "E56.13.0.2", {"start": v(-66, 10) * mm, "end": v(-67, 12) * mm});
            skLineSegment(sketch, "E56.13.0.3", {"start": v(-67, 12) * mm, "end": v(-63.5, 12) * mm});
            skLineSegment(sketch, "E56.14.0.0", {"start": v(-68, 12) * mm, "end": v(-69, 10) * mm});
            skLineSegment(sketch, "E56.14.0.1", {"start": v(-69, 10) * mm, "end": v(-70.5, 10) * mm});
            skLineSegment(sketch, "E56.14.0.2", {"start": v(-70.5, 10) * mm, "end": v(-71.5, 12) * mm});
            skLineSegment(sketch, "E56.14.0.3", {"start": v(-71.5, 12) * mm, "end": v(-68, 12) * mm});
            skLineSegment(sketch, "E56.15.0.0", {"start": v(-72.5, 12) * mm, "end": v(-73.5, 10) * mm});
            skLineSegment(sketch, "E56.15.0.1", {"start": v(-73.5, 10) * mm, "end": v(-75, 10) * mm});
            skLineSegment(sketch, "E56.15.0.2", {"start": v(-75, 10) * mm, "end": v(-76, 12) * mm});
            skLineSegment(sketch, "E56.15.0.3", {"start": v(-76, 12) * mm, "end": v(-72.5, 12) * mm});
            skLineSegment(sketch, "E56.16.0.0", {"start": v(-77, 12) * mm, "end": v(-78, 10) * mm});
            skLineSegment(sketch, "E56.16.0.1", {"start": v(-78, 10) * mm, "end": v(-79.5, 10) * mm});
            skLineSegment(sketch, "E56.16.0.2", {"start": v(-79.5, 10) * mm, "end": v(-80.5, 12) * mm});
            skLineSegment(sketch, "E56.16.0.3", {"start": v(-80.5, 12) * mm, "end": v(-77, 12) * mm});
            skLineSegment(sketch, "E56.17.0.0", {"start": v(-81.5, 12) * mm, "end": v(-82.5, 10) * mm});
            skLineSegment(sketch, "E56.17.0.1", {"start": v(-82.5, 10) * mm, "end": v(-84, 10) * mm});
            skLineSegment(sketch, "E56.17.0.2", {"start": v(-84, 10) * mm, "end": v(-85, 12) * mm});
            skLineSegment(sketch, "E56.17.0.3", {"start": v(-85, 12) * mm, "end": v(-81.5, 12) * mm});
            skLineSegment(sketch, "E56.18.0.0", {"start": v(-86, 12) * mm, "end": v(-87, 10) * mm});
            skLineSegment(sketch, "E56.18.0.1", {"start": v(-87, 10) * mm, "end": v(-88.5, 10) * mm});
            skLineSegment(sketch, "E56.18.0.2", {"start": v(-88.5, 10) * mm, "end": v(-89.5, 12) * mm});
            skLineSegment(sketch, "E56.18.0.3", {"start": v(-89.5, 12) * mm, "end": v(-86, 12) * mm});
            skLineSegment(sketch, "E56.direction1", {"start": v(-7.5, 10) * mm, "end": v(-12, 10) * mm, "construction": true});
            skLineSegment(sketch, "E57", {"start": v(1.3, 5) * mm, "end": v(-117.54, 5) * mm, "construction": true});
            skLineSegment(sketch, "E58.MirrorCS", {"start": v(-15, 0) * mm, "end": v(-16.5, 0) * mm});
            skLineSegment(sketch, "E59.MirrorCS", {"start": v(-12, 0) * mm, "end": v(-13, -2) * mm});
            skLineSegment(sketch, "E60.MirrorCS", {"start": v(-10.5, 0) * mm, "end": v(-12, 0) * mm});
            skLineSegment(sketch, "E61.MirrorCS", {"start": v(-9.5, -2) * mm, "end": v(-10.5, 0) * mm});
            skLineSegment(sketch, "E62.MirrorCS", {"start": v(-7.5, 0) * mm, "end": v(-8.5, -2) * mm});
            skLineSegment(sketch, "E63.MirrorCS", {"start": v(-6, 0) * mm, "end": v(-7.5, 0) * mm});
            skLineSegment(sketch, "E64.MirrorCS", {"start": v(-5, -2) * mm, "end": v(-6, 0) * mm});
            skLineSegment(sketch, "E65.MirrorCS", {"start": v(-21, 0) * mm, "end": v(-22, -2) * mm});
            skLineSegment(sketch, "E66.MirrorCS", {"start": v(-19.5, 0) * mm, "end": v(-21, 0) * mm});
            skLineSegment(sketch, "E67.MirrorCS", {"start": v(-48, 0) * mm, "end": v(-49, -2) * mm});
            skLineSegment(sketch, "E68.MirrorCS", {"start": v(-66, 0) * mm, "end": v(-67, -2) * mm});
            skLineSegment(sketch, "E69.MirrorCS", {"start": v(-84, 0) * mm, "end": v(-85, -2) * mm});
            skLineSegment(sketch, "E70.MirrorCS", {"start": v(-30, 0) * mm, "end": v(-31, -2) * mm});
            skLineSegment(sketch, "E71.MirrorCS", {"start": v(-7.5, 0) * mm, "end": v(-12, 0) * mm, "construction": true});
            skLineSegment(sketch, "E72.MirrorCS", {"start": v(-36.5, -2) * mm, "end": v(-37.5, 0) * mm});
            skLineSegment(sketch, "E73.MirrorCS", {"start": v(-54.5, -2) * mm, "end": v(-55.5, 0) * mm});
            skLineSegment(sketch, "E74.MirrorCS", {"start": v(-72.5, -2) * mm, "end": v(-73.5, 0) * mm});
            skLineSegment(sketch, "E75.MirrorCS", {"start": v(-39, 0) * mm, "end": v(-40, -2) * mm});
            skLineSegment(sketch, "E76.MirrorCS", {"start": v(-46.5, 0) * mm, "end": v(-48, 0) * mm});
            skLineSegment(sketch, "E77.MirrorCS", {"start": v(-57, 0) * mm, "end": v(-58, -2) * mm});
            skLineSegment(sketch, "E78.MirrorCS", {"start": v(-64.5, 0) * mm, "end": v(-66, 0) * mm});
            skLineSegment(sketch, "E79.MirrorCS", {"start": v(-82.5, 0) * mm, "end": v(-84, 0) * mm});
            skLineSegment(sketch, "E80.MirrorCS", {"start": v(-75, 0) * mm, "end": v(-76, -2) * mm});
            skLineSegment(sketch, "E81.MirrorCS", {"start": v(-28.5, 0) * mm, "end": v(-30, 0) * mm});
            skLineSegment(sketch, "E82.MirrorCS", {"start": v(-45.5, -2) * mm, "end": v(-46.5, 0) * mm});
            skLineSegment(sketch, "E83.MirrorCS", {"start": v(-37.5, 0) * mm, "end": v(-39, 0) * mm});
            skLineSegment(sketch, "E84.MirrorCS", {"start": v(-63.5, -2) * mm, "end": v(-64.5, 0) * mm});
            skLineSegment(sketch, "E85.MirrorCS", {"start": v(-55.5, 0) * mm, "end": v(-57, 0) * mm});
            skLineSegment(sketch, "E86.MirrorCS", {"start": v(-81.5, -2) * mm, "end": v(-82.5, 0) * mm});
            skLineSegment(sketch, "E87.MirrorCS", {"start": v(-73.5, 0) * mm, "end": v(-75, 0) * mm});
            skLineSegment(sketch, "E88.MirrorCS", {"start": v(-27.5, -2) * mm, "end": v(-28.5, 0) * mm});
            skLineSegment(sketch, "E89.MirrorCS", {"start": v(-88.5, 0) * mm, "end": v(-89.5, -2) * mm});
            skLineSegment(sketch, "E90.MirrorCS", {"start": v(-34.5, 0) * mm, "end": v(-35.5, -2) * mm});
            skLineSegment(sketch, "E91.MirrorCS", {"start": v(-52.5, 0) * mm, "end": v(-53.5, -2) * mm});
            skLineSegment(sketch, "E92.MirrorCS", {"start": v(-70.5, 0) * mm, "end": v(-71.5, -2) * mm});
            skLineSegment(sketch, "E93.MirrorCS", {"start": v(-33, 0) * mm, "end": v(-34.5, 0) * mm});
            skLineSegment(sketch, "E94.MirrorCS", {"start": v(-51, 0) * mm, "end": v(-52.5, 0) * mm});
            skLineSegment(sketch, "E95.MirrorCS", {"start": v(-69, 0) * mm, "end": v(-70.5, 0) * mm});
            skLineSegment(sketch, "E96.MirrorCS", {"start": v(-43.5, 0) * mm, "end": v(-44.5, -2) * mm});
            skLineSegment(sketch, "E97.MirrorCS", {"start": v(-61.5, 0) * mm, "end": v(-62.5, -2) * mm});
            skLineSegment(sketch, "E98.MirrorCS", {"start": v(-79.5, 0) * mm, "end": v(-80.5, -2) * mm});
            skLineSegment(sketch, "E99.MirrorCS", {"start": v(-87, 0) * mm, "end": v(-88.5, 0) * mm});
            skLineSegment(sketch, "E100.MirrorCS", {"start": v(-25.5, 0) * mm, "end": v(-26.5, -2) * mm});
            skLineSegment(sketch, "E101.MirrorCS", {"start": v(-42, 0) * mm, "end": v(-43.5, 0) * mm});
            skLineSegment(sketch, "E102.MirrorCS", {"start": v(-60, 0) * mm, "end": v(-61.5, 0) * mm});
            skLineSegment(sketch, "E103.MirrorCS", {"start": v(-59, -2) * mm, "end": v(-60, 0) * mm});
            skLineSegment(sketch, "E104.MirrorCS", {"start": v(-32, -2) * mm, "end": v(-33, 0) * mm});
            skLineSegment(sketch, "E105.MirrorCS", {"start": v(-24, 0) * mm, "end": v(-25.5, 0) * mm});
            skLineSegment(sketch, "E106.MirrorCS", {"start": v(-41, -2) * mm, "end": v(-42, 0) * mm});
            skLineSegment(sketch, "E107.MirrorCS", {"start": v(-68, -2) * mm, "end": v(-69, 0) * mm});
            skLineSegment(sketch, "E108.MirrorCS", {"start": v(-18.5, -2) * mm, "end": v(-19.5, 0) * mm});
            skLineSegment(sketch, "E109.MirrorCS", {"start": v(-14, -2) * mm, "end": v(-15, 0) * mm});
            skLineSegment(sketch, "E110.MirrorCS", {"start": v(-50, -2) * mm, "end": v(-51, 0) * mm});
            skLineSegment(sketch, "E111.MirrorCS", {"start": v(-86, -2) * mm, "end": v(-87, 0) * mm});
            skLineSegment(sketch, "E112.MirrorCS", {"start": v(-78, 0) * mm, "end": v(-79.5, 0) * mm});
            skLineSegment(sketch, "E113.MirrorCS", {"start": v(-23, -2) * mm, "end": v(-24, 0) * mm});
            skLineSegment(sketch, "E114.MirrorCS", {"start": v(-16.5, 0) * mm, "end": v(-17.5, -2) * mm});
            skLineSegment(sketch, "E115.MirrorCS", {"start": v(-77, -2) * mm, "end": v(-78, 0) * mm});
            skLineSegment(sketch, "E116.MirrorCS", {"start": v(-49, -2) * mm, "end": v(-45.5, -2) * mm});
            skLineSegment(sketch, "E117.MirrorCS", {"start": v(-31, -2) * mm, "end": v(-27.5, -2) * mm});
            skLineSegment(sketch, "E118.MirrorCS", {"start": v(-67, -2) * mm, "end": v(-63.5, -2) * mm});
            skLineSegment(sketch, "E119.MirrorCS", {"start": v(-13, -2) * mm, "end": v(-9.5, -2) * mm});
            skLineSegment(sketch, "E120.MirrorCS", {"start": v(-8.5, -2) * mm, "end": v(-5, -2) * mm});
            skLineSegment(sketch, "E121.MirrorCS", {"start": v(-22, -2) * mm, "end": v(-18.5, -2) * mm});
            skLineSegment(sketch, "E122.MirrorCS", {"start": v(-40, -2) * mm, "end": v(-36.5, -2) * mm});
            skLineSegment(sketch, "E123.MirrorCS", {"start": v(-58, -2) * mm, "end": v(-54.5, -2) * mm});
            skLineSegment(sketch, "E124.MirrorCS", {"start": v(-76, -2) * mm, "end": v(-72.5, -2) * mm});
            skLineSegment(sketch, "E125.MirrorCS", {"start": v(-89.5, -2) * mm, "end": v(-86, -2) * mm});
            skLineSegment(sketch, "E126.MirrorCS", {"start": v(-35.5, -2) * mm, "end": v(-32, -2) * mm});
            skLineSegment(sketch, "E127.MirrorCS", {"start": v(-53.5, -2) * mm, "end": v(-50, -2) * mm});
            skLineSegment(sketch, "E128.MirrorCS", {"start": v(-71.5, -2) * mm, "end": v(-68, -2) * mm});
            skLineSegment(sketch, "E129.MirrorCS", {"start": v(-44.5, -2) * mm, "end": v(-41, -2) * mm});
            skLineSegment(sketch, "E130.MirrorCS", {"start": v(-62.5, -2) * mm, "end": v(-59, -2) * mm});
            skLineSegment(sketch, "E131.MirrorCS", {"start": v(-80.5, -2) * mm, "end": v(-77, -2) * mm});
            skLineSegment(sketch, "E132.MirrorCS", {"start": v(-26.5, -2) * mm, "end": v(-23, -2) * mm});
            skLineSegment(sketch, "E133.MirrorCS", {"start": v(-17.5, -2) * mm, "end": v(-14, -2) * mm});
            skLineSegment(sketch, "E134.MirrorCS", {"start": v(-85, -2) * mm, "end": v(-81.5, -2) * mm});
            skSolve(sketch);
        }
        {
            var Q0;
            Q0=makeQuery(id+"F20.imprint","IMPRINT",FACE,{"disambiguationData":[TD([[makeQuery(id+"F20.imprint","IMPRINT",EDGE,{"derivedFrom":sQuery(id+"F20.wireOp",EDGE,"E56.18.0.0")}),-1.0]])]});
            var Q1;
            Q1=makeQuery(id+"F20.imprint","IMPRINT",FACE,{"disambiguationData":[TD([[makeQuery(id+"F20.imprint","IMPRINT",EDGE,{"derivedFrom":sQuery(id+"F20.wireOp",EDGE,"E56.17.0.0")}),-1.0]])]});
            var Q2;
            Q2=makeQuery(id+"F20.imprint","IMPRINT",FACE,{"disambiguationData":[TD([[makeQuery(id+"F20.imprint","IMPRINT",EDGE,{"derivedFrom":sQuery(id+"F20.wireOp",EDGE,"E56.16.0.0")}),-1.0]])]});
            var Q3;
            Q3=makeQuery(id+"F20.imprint","IMPRINT",FACE,{"disambiguationData":[TD([[makeQuery(id+"F20.imprint","IMPRINT",EDGE,{"derivedFrom":sQuery(id+"F20.wireOp",EDGE,"E56.15.0.0")}),-1.0]])]});
            var Q4;
            Q4=makeQuery(id+"F20.imprint","IMPRINT",FACE,{"disambiguationData":[TD([[makeQuery(id+"F20.imprint","IMPRINT",EDGE,{"derivedFrom":sQuery(id+"F20.wireOp",EDGE,"E56.14.0.0")}),-1.0]])]});
            var Q5;
            Q5=makeQuery(id+"F20.imprint","IMPRINT",FACE,{"disambiguationData":[TD([[makeQuery(id+"F20.imprint","IMPRINT",EDGE,{"derivedFrom":sQuery(id+"F20.wireOp",EDGE,"E56.13.0.0")}),-1.0]])]});
            var Q6;
            Q6=makeQuery(id+"F20.imprint","IMPRINT",FACE,{"disambiguationData":[TD([[makeQuery(id+"F20.imprint","IMPRINT",EDGE,{"derivedFrom":sQuery(id+"F20.wireOp",EDGE,"E56.12.0.0")}),-1.0]])]});
            var Q7;
            Q7=makeQuery(id+"F20.imprint","IMPRINT",FACE,{"disambiguationData":[TD([[makeQuery(id+"F20.imprint","IMPRINT",EDGE,{"derivedFrom":sQuery(id+"F20.wireOp",EDGE,"E56.11.0.0")}),-1.0]])]});
            var Q8;
            Q8=makeQuery(id+"F20.imprint","IMPRINT",FACE,{"disambiguationData":[TD([[makeQuery(id+"F20.imprint","IMPRINT",EDGE,{"derivedFrom":sQuery(id+"F20.wireOp",EDGE,"E56.10.0.0")}),-1.0]])]});
            var Q9;
            Q9=makeQuery(id+"F20.imprint","IMPRINT",FACE,{"disambiguationData":[TD([[makeQuery(id+"F20.imprint","IMPRINT",EDGE,{"derivedFrom":sQuery(id+"F20.wireOp",EDGE,"E56.9.0.0")}),-1.0]])]});
            var Q10;
            Q10=makeQuery(id+"F20.imprint","IMPRINT",FACE,{"disambiguationData":[TD([[makeQuery(id+"F20.imprint","IMPRINT",EDGE,{"derivedFrom":sQuery(id+"F20.wireOp",EDGE,"E56.8.0.0")}),-1.0]])]});
            var Q11;
            Q11=makeQuery(id+"F20.imprint","IMPRINT",FACE,{"disambiguationData":[TD([[makeQuery(id+"F20.imprint","IMPRINT",EDGE,{"derivedFrom":sQuery(id+"F20.wireOp",EDGE,"E56.7.0.0")}),-1.0]])]});
            var Q12;
            Q12=makeQuery(id+"F20.imprint","IMPRINT",FACE,{"disambiguationData":[TD([[makeQuery(id+"F20.imprint","IMPRINT",EDGE,{"derivedFrom":sQuery(id+"F20.wireOp",EDGE,"E56.6.0.0")}),-1.0]])]});
            var Q13;
            Q13=makeQuery(id+"F20.imprint","IMPRINT",FACE,{"disambiguationData":[TD([[makeQuery(id+"F20.imprint","IMPRINT",EDGE,{"derivedFrom":sQuery(id+"F20.wireOp",EDGE,"E56.5.0.0")}),-1.0]])]});
            var Q14;
            Q14=makeQuery(id+"F20.imprint","IMPRINT",FACE,{"disambiguationData":[TD([[makeQuery(id+"F20.imprint","IMPRINT",EDGE,{"derivedFrom":sQuery(id+"F20.wireOp",EDGE,"E56.4.0.0")}),-1.0]])]});
            var Q15;
            Q15=makeQuery(id+"F20.imprint","IMPRINT",FACE,{"disambiguationData":[TD([[makeQuery(id+"F20.imprint","IMPRINT",EDGE,{"derivedFrom":sQuery(id+"F20.wireOp",EDGE,"E56.3.0.0")}),-1.0]])]});
            var Q16;
            Q16=makeQuery(id+"F20.imprint","IMPRINT",FACE,{"disambiguationData":[TD([[makeQuery(id+"F20.imprint","IMPRINT",EDGE,{"derivedFrom":sQuery(id+"F20.wireOp",EDGE,"E56.2.0.0")}),-1.0]])]});
            var Q17;
            Q17=makeQuery(id+"F20.imprint","IMPRINT",FACE,{"disambiguationData":[TD([[makeQuery(id+"F20.imprint","IMPRINT",EDGE,{"derivedFrom":sQuery(id+"F20.wireOp",EDGE,"E56.1.0.0")}),-1.0]])]});
            var Q18;
            Q18=makeQuery(id+"F20.imprint","IMPRINT",FACE,{"disambiguationData":[TD([[makeQuery(id+"F20.imprint","IMPRINT",EDGE,{"derivedFrom":sQuery(id+"F20.wireOp",EDGE,"E52")}),-1.0]])]});
            var Q19;
            Q19=makeQuery(id+"F20.imprint","IMPRINT",FACE,{"disambiguationData":[TD([[makeQuery(id+"F20.imprint","IMPRINT",EDGE,{"derivedFrom":sQuery(id+"F20.wireOp",EDGE,"E89.MirrorCS")}),1.0]])]});
            var Q20;
            Q20=makeQuery(id+"F20.imprint","IMPRINT",FACE,{"disambiguationData":[TD([[makeQuery(id+"F20.imprint","IMPRINT",EDGE,{"derivedFrom":sQuery(id+"F20.wireOp",EDGE,"E69.MirrorCS")}),1.0]])]});
            var Q21;
            Q21=makeQuery(id+"F20.imprint","IMPRINT",FACE,{"disambiguationData":[TD([[makeQuery(id+"F20.imprint","IMPRINT",EDGE,{"derivedFrom":sQuery(id+"F20.wireOp",EDGE,"E98.MirrorCS")}),1.0]])]});
            var Q22;
            Q22=makeQuery(id+"F20.imprint","IMPRINT",FACE,{"disambiguationData":[TD([[makeQuery(id+"F20.imprint","IMPRINT",EDGE,{"derivedFrom":sQuery(id+"F20.wireOp",EDGE,"E74.MirrorCS")}),1.0]])]});
            var Q23;
            Q23=makeQuery(id+"F20.imprint","IMPRINT",FACE,{"disambiguationData":[TD([[makeQuery(id+"F20.imprint","IMPRINT",EDGE,{"derivedFrom":sQuery(id+"F20.wireOp",EDGE,"E92.MirrorCS")}),1.0]])]});
            var Q24;
            Q24=makeQuery(id+"F20.imprint","IMPRINT",FACE,{"disambiguationData":[TD([[makeQuery(id+"F20.imprint","IMPRINT",EDGE,{"derivedFrom":sQuery(id+"F20.wireOp",EDGE,"E68.MirrorCS")}),1.0]])]});
            var Q25;
            Q25=makeQuery(id+"F20.imprint","IMPRINT",FACE,{"disambiguationData":[TD([[makeQuery(id+"F20.imprint","IMPRINT",EDGE,{"derivedFrom":sQuery(id+"F20.wireOp",EDGE,"E97.MirrorCS")}),1.0]])]});
            var Q26;
            Q26=makeQuery(id+"F20.imprint","IMPRINT",FACE,{"disambiguationData":[TD([[makeQuery(id+"F20.imprint","IMPRINT",EDGE,{"derivedFrom":sQuery(id+"F20.wireOp",EDGE,"E73.MirrorCS")}),1.0]])]});
            var Q27;
            Q27=makeQuery(id+"F20.imprint","IMPRINT",FACE,{"disambiguationData":[TD([[makeQuery(id+"F20.imprint","IMPRINT",EDGE,{"derivedFrom":sQuery(id+"F20.wireOp",EDGE,"E91.MirrorCS")}),1.0]])]});
            var Q28;
            Q28=makeQuery(id+"F20.imprint","IMPRINT",FACE,{"disambiguationData":[TD([[makeQuery(id+"F20.imprint","IMPRINT",EDGE,{"derivedFrom":sQuery(id+"F20.wireOp",EDGE,"E67.MirrorCS")}),1.0]])]});
            var Q29;
            Q29=makeQuery(id+"F20.imprint","IMPRINT",FACE,{"disambiguationData":[TD([[makeQuery(id+"F20.imprint","IMPRINT",EDGE,{"derivedFrom":sQuery(id+"F20.wireOp",EDGE,"E96.MirrorCS")}),1.0]])]});
            var Q30;
            Q30=makeQuery(id+"F20.imprint","IMPRINT",FACE,{"disambiguationData":[TD([[makeQuery(id+"F20.imprint","IMPRINT",EDGE,{"derivedFrom":sQuery(id+"F20.wireOp",EDGE,"E72.MirrorCS")}),1.0]])]});
            var Q31;
            Q31=makeQuery(id+"F20.imprint","IMPRINT",FACE,{"disambiguationData":[TD([[makeQuery(id+"F20.imprint","IMPRINT",EDGE,{"derivedFrom":sQuery(id+"F20.wireOp",EDGE,"E90.MirrorCS")}),1.0]])]});
            var Q32;
            Q32=makeQuery(id+"F20.imprint","IMPRINT",FACE,{"disambiguationData":[TD([[makeQuery(id+"F20.imprint","IMPRINT",EDGE,{"derivedFrom":sQuery(id+"F20.wireOp",EDGE,"E70.MirrorCS")}),1.0]])]});
            var Q33;
            Q33=makeQuery(id+"F20.imprint","IMPRINT",FACE,{"disambiguationData":[TD([[makeQuery(id+"F20.imprint","IMPRINT",EDGE,{"derivedFrom":sQuery(id+"F20.wireOp",EDGE,"E100.MirrorCS")}),1.0]])]});
            var Q34;
            Q34=makeQuery(id+"F20.imprint","IMPRINT",FACE,{"disambiguationData":[TD([[makeQuery(id+"F20.imprint","IMPRINT",EDGE,{"derivedFrom":sQuery(id+"F20.wireOp",EDGE,"E65.MirrorCS")}),1.0]])]});
            var Q35;
            Q35=makeQuery(id+"F20.imprint","IMPRINT",FACE,{"disambiguationData":[TD([[makeQuery(id+"F20.imprint","IMPRINT",EDGE,{"derivedFrom":sQuery(id+"F20.wireOp",EDGE,"E58.MirrorCS")}),1.0]])]});
            var Q36;
            Q36=makeQuery(id+"F20.imprint","IMPRINT",FACE,{"disambiguationData":[TD([[makeQuery(id+"F20.imprint","IMPRINT",EDGE,{"derivedFrom":sQuery(id+"F20.wireOp",EDGE,"E59.MirrorCS")}),1.0]])]});
            var Q37;
            Q37=makeQuery(id+"F20.imprint","IMPRINT",FACE,{"disambiguationData":[TD([[makeQuery(id+"F20.imprint","IMPRINT",EDGE,{"derivedFrom":sQuery(id+"F20.wireOp",EDGE,"E62.MirrorCS")}),1.0]])]});
            extrude(context, id + "F21", {"entities" : qUnion([Q0, Q1, Q2, Q3, Q4, Q5, Q6, Q7, Q8, Q9, Q10, Q11, Q12, Q13, Q14, Q15, Q16, Q17, Q18, Q19, Q20, Q21, Q22, Q23, Q24, Q25, Q26, Q27, Q28, Q29, Q30, Q31, Q32, Q33, Q34, Q35, Q36, Q37]), "operationType" : NewBodyOperationType.REMOVE, "oppositeDirection" : true, "depth" : 8 * mm, "offsetDistance" : 25 * mm});
        }
        {
            var Q0;
            Q0=makeQuery(id+"F7.boolean.opBoolean","MERGE",FACE,{"derivedFrom":[makeQuery(id+"F1.opExtrude","SWEPT_FACE",FACE,{"disambiguationData":[OSD([sQuery(id+"F0.wireOp",EDGE,"E0.right")])]}),makeQuery(id+"F7.opExtrude","SWEPT_FACE",FACE,{"disambiguationData":[OSD([sQuery(id+"F6.wireOp",EDGE,"E26")])]})]});
            var sketch = newSketch(context, id + "F22", { "sketchPlane" : qUnion([Q0])});
            skLineSegment(sketch, "E135", {"start": v(5, 12) * mm, "end": v(6, 10) * mm});
            skLineSegment(sketch, "E136", {"start": v(6, 10) * mm, "end": v(7.5, 10) * mm});
            skLineSegment(sketch, "E137", {"start": v(7.5, 10) * mm, "end": v(8.5, 12) * mm});
            skLineSegment(sketch, "E138", {"start": v(5, 12) * mm, "end": v(8.5, 12) * mm});
            skLineSegment(sketch, "E139.1.0.0", {"start": v(9.5, 12) * mm, "end": v(10.5, 10) * mm});
            skLineSegment(sketch, "E139.1.0.1", {"start": v(9.5, 12) * mm, "end": v(13, 12) * mm});
            skLineSegment(sketch, "E139.1.0.2", {"start": v(12, 10) * mm, "end": v(13, 12) * mm});
            skLineSegment(sketch, "E139.1.0.3", {"start": v(10.5, 10) * mm, "end": v(12, 10) * mm});
            skLineSegment(sketch, "E139.2.0.0", {"start": v(14, 12) * mm, "end": v(15, 10) * mm});
            skLineSegment(sketch, "E139.2.0.1", {"start": v(14, 12) * mm, "end": v(17.5, 12) * mm});
            skLineSegment(sketch, "E139.2.0.2", {"start": v(16.5, 10) * mm, "end": v(17.5, 12) * mm});
            skLineSegment(sketch, "E139.2.0.3", {"start": v(15, 10) * mm, "end": v(16.5, 10) * mm});
            skLineSegment(sketch, "E139.3.0.0", {"start": v(18.5, 12) * mm, "end": v(19.5, 10) * mm});
            skLineSegment(sketch, "E139.3.0.1", {"start": v(18.5, 12) * mm, "end": v(22, 12) * mm});
            skLineSegment(sketch, "E139.3.0.2", {"start": v(21, 10) * mm, "end": v(22, 12) * mm});
            skLineSegment(sketch, "E139.3.0.3", {"start": v(19.5, 10) * mm, "end": v(21, 10) * mm});
            skLineSegment(sketch, "E139.4.0.0", {"start": v(23, 12) * mm, "end": v(24, 10) * mm});
            skLineSegment(sketch, "E139.4.0.1", {"start": v(23, 12) * mm, "end": v(26.5, 12) * mm});
            skLineSegment(sketch, "E139.4.0.2", {"start": v(25.5, 10) * mm, "end": v(26.5, 12) * mm});
            skLineSegment(sketch, "E139.4.0.3", {"start": v(24, 10) * mm, "end": v(25.5, 10) * mm});
            skLineSegment(sketch, "E139.5.0.0", {"start": v(27.5, 12) * mm, "end": v(28.5, 10) * mm});
            skLineSegment(sketch, "E139.5.0.1", {"start": v(27.5, 12) * mm, "end": v(31, 12) * mm});
            skLineSegment(sketch, "E139.5.0.2", {"start": v(30, 10) * mm, "end": v(31, 12) * mm});
            skLineSegment(sketch, "E139.5.0.3", {"start": v(28.5, 10) * mm, "end": v(30, 10) * mm});
            skLineSegment(sketch, "E139.6.0.0", {"start": v(32, 12) * mm, "end": v(33, 10) * mm});
            skLineSegment(sketch, "E139.6.0.1", {"start": v(32, 12) * mm, "end": v(35.5, 12) * mm});
            skLineSegment(sketch, "E139.6.0.2", {"start": v(34.5, 10) * mm, "end": v(35.5, 12) * mm});
            skLineSegment(sketch, "E139.6.0.3", {"start": v(33, 10) * mm, "end": v(34.5, 10) * mm});
            skLineSegment(sketch, "E139.7.0.0", {"start": v(36.5, 12) * mm, "end": v(37.5, 10) * mm});
            skLineSegment(sketch, "E139.7.0.1", {"start": v(36.5, 12) * mm, "end": v(40, 12) * mm});
            skLineSegment(sketch, "E139.7.0.2", {"start": v(39, 10) * mm, "end": v(40, 12) * mm});
            skLineSegment(sketch, "E139.7.0.3", {"start": v(37.5, 10) * mm, "end": v(39, 10) * mm});
            skLineSegment(sketch, "E139.8.0.0", {"start": v(41, 12) * mm, "end": v(42, 10) * mm});
            skLineSegment(sketch, "E139.8.0.1", {"start": v(41, 12) * mm, "end": v(44.5, 12) * mm});
            skLineSegment(sketch, "E139.8.0.2", {"start": v(43.5, 10) * mm, "end": v(44.5, 12) * mm});
            skLineSegment(sketch, "E139.8.0.3", {"start": v(42, 10) * mm, "end": v(43.5, 10) * mm});
            skLineSegment(sketch, "E139.9.0.0", {"start": v(45.5, 12) * mm, "end": v(46.5, 10) * mm});
            skLineSegment(sketch, "E139.9.0.1", {"start": v(45.5, 12) * mm, "end": v(49, 12) * mm});
            skLineSegment(sketch, "E139.9.0.2", {"start": v(48, 10) * mm, "end": v(49, 12) * mm});
            skLineSegment(sketch, "E139.9.0.3", {"start": v(46.5, 10) * mm, "end": v(48, 10) * mm});
            skLineSegment(sketch, "E139.10.0.0", {"start": v(50, 12) * mm, "end": v(51, 10) * mm});
            skLineSegment(sketch, "E139.10.0.1", {"start": v(50, 12) * mm, "end": v(53.5, 12) * mm});
            skLineSegment(sketch, "E139.10.0.2", {"start": v(52.5, 10) * mm, "end": v(53.5, 12) * mm});
            skLineSegment(sketch, "E139.10.0.3", {"start": v(51, 10) * mm, "end": v(52.5, 10) * mm});
            skLineSegment(sketch, "E139.11.0.0", {"start": v(54.5, 12) * mm, "end": v(55.5, 10) * mm});
            skLineSegment(sketch, "E139.11.0.1", {"start": v(54.5, 12) * mm, "end": v(58, 12) * mm});
            skLineSegment(sketch, "E139.11.0.2", {"start": v(57, 10) * mm, "end": v(58, 12) * mm});
            skLineSegment(sketch, "E139.11.0.3", {"start": v(55.5, 10) * mm, "end": v(57, 10) * mm});
            skLineSegment(sketch, "E139.12.0.0", {"start": v(59, 12) * mm, "end": v(60, 10) * mm});
            skLineSegment(sketch, "E139.12.0.1", {"start": v(59, 12) * mm, "end": v(62.5, 12) * mm});
            skLineSegment(sketch, "E139.12.0.2", {"start": v(61.5, 10) * mm, "end": v(62.5, 12) * mm});
            skLineSegment(sketch, "E139.12.0.3", {"start": v(60, 10) * mm, "end": v(61.5, 10) * mm});
            skLineSegment(sketch, "E139.13.0.0", {"start": v(63.5, 12) * mm, "end": v(64.5, 10) * mm});
            skLineSegment(sketch, "E139.13.0.1", {"start": v(63.5, 12) * mm, "end": v(67, 12) * mm});
            skLineSegment(sketch, "E139.13.0.2", {"start": v(66, 10) * mm, "end": v(67, 12) * mm});
            skLineSegment(sketch, "E139.13.0.3", {"start": v(64.5, 10) * mm, "end": v(66, 10) * mm});
            skLineSegment(sketch, "E139.14.0.0", {"start": v(68, 12) * mm, "end": v(69, 10) * mm});
            skLineSegment(sketch, "E139.14.0.1", {"start": v(68, 12) * mm, "end": v(71.5, 12) * mm});
            skLineSegment(sketch, "E139.14.0.2", {"start": v(70.5, 10) * mm, "end": v(71.5, 12) * mm});
            skLineSegment(sketch, "E139.14.0.3", {"start": v(69, 10) * mm, "end": v(70.5, 10) * mm});
            skLineSegment(sketch, "E139.15.0.0", {"start": v(72.5, 12) * mm, "end": v(73.5, 10) * mm});
            skLineSegment(sketch, "E139.15.0.1", {"start": v(72.5, 12) * mm, "end": v(76, 12) * mm});
            skLineSegment(sketch, "E139.15.0.2", {"start": v(75, 10) * mm, "end": v(76, 12) * mm});
            skLineSegment(sketch, "E139.15.0.3", {"start": v(73.5, 10) * mm, "end": v(75, 10) * mm});
            skLineSegment(sketch, "E139.16.0.0", {"start": v(77, 12) * mm, "end": v(78, 10) * mm});
            skLineSegment(sketch, "E139.16.0.1", {"start": v(77, 12) * mm, "end": v(80.5, 12) * mm});
            skLineSegment(sketch, "E139.16.0.2", {"start": v(79.5, 10) * mm, "end": v(80.5, 12) * mm});
            skLineSegment(sketch, "E139.16.0.3", {"start": v(78, 10) * mm, "end": v(79.5, 10) * mm});
            skLineSegment(sketch, "E139.17.0.0", {"start": v(81.5, 12) * mm, "end": v(82.5, 10) * mm});
            skLineSegment(sketch, "E139.17.0.1", {"start": v(81.5, 12) * mm, "end": v(85, 12) * mm});
            skLineSegment(sketch, "E139.17.0.2", {"start": v(84, 10) * mm, "end": v(85, 12) * mm});
            skLineSegment(sketch, "E139.17.0.3", {"start": v(82.5, 10) * mm, "end": v(84, 10) * mm});
            skLineSegment(sketch, "E139.18.0.0", {"start": v(86, 12) * mm, "end": v(87, 10) * mm});
            skLineSegment(sketch, "E139.18.0.1", {"start": v(86, 12) * mm, "end": v(89.5, 12) * mm});
            skLineSegment(sketch, "E139.18.0.2", {"start": v(88.5, 10) * mm, "end": v(89.5, 12) * mm});
            skLineSegment(sketch, "E139.18.0.3", {"start": v(87, 10) * mm, "end": v(88.5, 10) * mm});
            skLineSegment(sketch, "E139.direction1", {"start": v(6, 10) * mm, "end": v(10.5, 10) * mm, "construction": true});
            skLineSegment(sketch, "E140", {"start": v(-5.22, 5) * mm, "end": v(110.16, 5) * mm, "construction": true});
            skLineSegment(sketch, "E141.MirrorCS", {"start": v(10.5, 0) * mm, "end": v(12, 0) * mm});
            skLineSegment(sketch, "E142.MirrorCS", {"start": v(6, 0) * mm, "end": v(7.5, 0) * mm});
            skLineSegment(sketch, "E143.MirrorCS", {"start": v(25.5, 0) * mm, "end": v(26.5, -2) * mm});
            skLineSegment(sketch, "E144.MirrorCS", {"start": v(86, -2) * mm, "end": v(87, 0) * mm});
            skLineSegment(sketch, "E145.MirrorCS", {"start": v(32, -2) * mm, "end": v(33, 0) * mm});
            skLineSegment(sketch, "E146.MirrorCS", {"start": v(50, -2) * mm, "end": v(51, 0) * mm});
            skLineSegment(sketch, "E147.MirrorCS", {"start": v(68, -2) * mm, "end": v(69, 0) * mm});
            skLineSegment(sketch, "E148.MirrorCS", {"start": v(41, -2) * mm, "end": v(42, 0) * mm});
            skLineSegment(sketch, "E149.MirrorCS", {"start": v(59, -2) * mm, "end": v(60, 0) * mm});
            skLineSegment(sketch, "E150.MirrorCS", {"start": v(77, -2) * mm, "end": v(78, 0) * mm});
            skLineSegment(sketch, "E151.MirrorCS", {"start": v(23, -2) * mm, "end": v(24, 0) * mm});
            skLineSegment(sketch, "E152.MirrorCS", {"start": v(82.5, 0) * mm, "end": v(84, 0) * mm});
            skLineSegment(sketch, "E153.MirrorCS", {"start": v(28.5, 0) * mm, "end": v(30, 0) * mm});
            skLineSegment(sketch, "E154.MirrorCS", {"start": v(46.5, 0) * mm, "end": v(48, 0) * mm});
            skLineSegment(sketch, "E155.MirrorCS", {"start": v(64.5, 0) * mm, "end": v(66, 0) * mm});
            skLineSegment(sketch, "E156.MirrorCS", {"start": v(37.5, 0) * mm, "end": v(39, 0) * mm});
            skLineSegment(sketch, "E157.MirrorCS", {"start": v(48, 0) * mm, "end": v(49, -2) * mm});
            skLineSegment(sketch, "E158.MirrorCS", {"start": v(66, 0) * mm, "end": v(67, -2) * mm});
            skLineSegment(sketch, "E159.MirrorCS", {"start": v(55.5, 0) * mm, "end": v(57, 0) * mm});
            skLineSegment(sketch, "E160.MirrorCS", {"start": v(84, 0) * mm, "end": v(85, -2) * mm});
            skLineSegment(sketch, "E161.MirrorCS", {"start": v(73.5, 0) * mm, "end": v(75, 0) * mm});
            skLineSegment(sketch, "E162.MirrorCS", {"start": v(30, 0) * mm, "end": v(31, -2) * mm});
            skLineSegment(sketch, "E163.MirrorCS", {"start": v(36.5, -2) * mm, "end": v(37.5, 0) * mm});
            skLineSegment(sketch, "E164.MirrorCS", {"start": v(54.5, -2) * mm, "end": v(55.5, 0) * mm});
            skLineSegment(sketch, "E165.MirrorCS", {"start": v(72.5, -2) * mm, "end": v(73.5, 0) * mm});
            skLineSegment(sketch, "E166.MirrorCS", {"start": v(39, 0) * mm, "end": v(40, -2) * mm});
            skLineSegment(sketch, "E167.MirrorCS", {"start": v(57, 0) * mm, "end": v(58, -2) * mm});
            skLineSegment(sketch, "E168.MirrorCS", {"start": v(75, 0) * mm, "end": v(76, -2) * mm});
            skLineSegment(sketch, "E169.MirrorCS", {"start": v(87, 0) * mm, "end": v(88.5, 0) * mm});
            skLineSegment(sketch, "E170.MirrorCS", {"start": v(33, 0) * mm, "end": v(34.5, 0) * mm});
            skLineSegment(sketch, "E171.MirrorCS", {"start": v(51, 0) * mm, "end": v(52.5, 0) * mm});
            skLineSegment(sketch, "E172.MirrorCS", {"start": v(69, 0) * mm, "end": v(70.5, 0) * mm});
            skLineSegment(sketch, "E173.MirrorCS", {"start": v(45.5, -2) * mm, "end": v(46.5, 0) * mm});
            skLineSegment(sketch, "E174.MirrorCS", {"start": v(63.5, -2) * mm, "end": v(64.5, 0) * mm});
            skLineSegment(sketch, "E175.MirrorCS", {"start": v(81.5, -2) * mm, "end": v(82.5, 0) * mm});
            skLineSegment(sketch, "E176.MirrorCS", {"start": v(27.5, -2) * mm, "end": v(28.5, 0) * mm});
            skLineSegment(sketch, "E177.MirrorCS", {"start": v(34.5, 0) * mm, "end": v(35.5, -2) * mm});
            skLineSegment(sketch, "E178.MirrorCS", {"start": v(52.5, 0) * mm, "end": v(53.5, -2) * mm});
            skLineSegment(sketch, "E179.MirrorCS", {"start": v(70.5, 0) * mm, "end": v(71.5, -2) * mm});
            skLineSegment(sketch, "E180.MirrorCS", {"start": v(42, 0) * mm, "end": v(43.5, 0) * mm});
            skLineSegment(sketch, "E181.MirrorCS", {"start": v(60, 0) * mm, "end": v(61.5, 0) * mm});
            skLineSegment(sketch, "E182.MirrorCS", {"start": v(78, 0) * mm, "end": v(79.5, 0) * mm});
            skLineSegment(sketch, "E183.MirrorCS", {"start": v(18.5, -2) * mm, "end": v(19.5, 0) * mm});
            skLineSegment(sketch, "E184.MirrorCS", {"start": v(15, 0) * mm, "end": v(16.5, 0) * mm});
            skLineSegment(sketch, "E185.MirrorCS", {"start": v(16.5, 0) * mm, "end": v(17.5, -2) * mm});
            skLineSegment(sketch, "E186.MirrorCS", {"start": v(88.5, 0) * mm, "end": v(89.5, -2) * mm});
            skLineSegment(sketch, "E187.MirrorCS", {"start": v(14, -2) * mm, "end": v(15, 0) * mm});
            skLineSegment(sketch, "E188.MirrorCS", {"start": v(12, 0) * mm, "end": v(13, -2) * mm});
            skLineSegment(sketch, "E189.MirrorCS", {"start": v(43.5, 0) * mm, "end": v(44.5, -2) * mm});
            skLineSegment(sketch, "E190.MirrorCS", {"start": v(5, -2) * mm, "end": v(6, 0) * mm});
            skLineSegment(sketch, "E191.MirrorCS", {"start": v(24, 0) * mm, "end": v(25.5, 0) * mm});
            skLineSegment(sketch, "E192.MirrorCS", {"start": v(7.5, 0) * mm, "end": v(8.5, -2) * mm});
            skLineSegment(sketch, "E193.MirrorCS", {"start": v(9.5, -2) * mm, "end": v(10.5, 0) * mm});
            skLineSegment(sketch, "E194.MirrorCS", {"start": v(79.5, 0) * mm, "end": v(80.5, -2) * mm});
            skLineSegment(sketch, "E195.MirrorCS", {"start": v(19.5, 0) * mm, "end": v(21, 0) * mm});
            skLineSegment(sketch, "E196.MirrorCS", {"start": v(61.5, 0) * mm, "end": v(62.5, -2) * mm});
            skLineSegment(sketch, "E197.MirrorCS", {"start": v(21, 0) * mm, "end": v(22, -2) * mm});
            skLineSegment(sketch, "E198.MirrorCS", {"start": v(9.5, -2) * mm, "end": v(13, -2) * mm});
            skLineSegment(sketch, "E199.MirrorCS", {"start": v(86, -2) * mm, "end": v(89.5, -2) * mm});
            skLineSegment(sketch, "E200.MirrorCS", {"start": v(32, -2) * mm, "end": v(35.5, -2) * mm});
            skLineSegment(sketch, "E201.MirrorCS", {"start": v(41, -2) * mm, "end": v(44.5, -2) * mm});
            skLineSegment(sketch, "E202.MirrorCS", {"start": v(59, -2) * mm, "end": v(62.5, -2) * mm});
            skLineSegment(sketch, "E203.MirrorCS", {"start": v(77, -2) * mm, "end": v(80.5, -2) * mm});
            skLineSegment(sketch, "E204.MirrorCS", {"start": v(23, -2) * mm, "end": v(26.5, -2) * mm});
            skLineSegment(sketch, "E205.MirrorCS", {"start": v(6, 0) * mm, "end": v(10.5, 0) * mm, "construction": true});
            skLineSegment(sketch, "E206.MirrorCS", {"start": v(45.5, -2) * mm, "end": v(49, -2) * mm});
            skLineSegment(sketch, "E207.MirrorCS", {"start": v(63.5, -2) * mm, "end": v(67, -2) * mm});
            skLineSegment(sketch, "E208.MirrorCS", {"start": v(81.5, -2) * mm, "end": v(85, -2) * mm});
            skLineSegment(sketch, "E209.MirrorCS", {"start": v(27.5, -2) * mm, "end": v(31, -2) * mm});
            skLineSegment(sketch, "E210.MirrorCS", {"start": v(36.5, -2) * mm, "end": v(40, -2) * mm});
            skLineSegment(sketch, "E211.MirrorCS", {"start": v(54.5, -2) * mm, "end": v(58, -2) * mm});
            skLineSegment(sketch, "E212.MirrorCS", {"start": v(50, -2) * mm, "end": v(53.5, -2) * mm});
            skLineSegment(sketch, "E213.MirrorCS", {"start": v(72.5, -2) * mm, "end": v(76, -2) * mm});
            skLineSegment(sketch, "E214.MirrorCS", {"start": v(68, -2) * mm, "end": v(71.5, -2) * mm});
            skLineSegment(sketch, "E215.MirrorCS", {"start": v(14, -2) * mm, "end": v(17.5, -2) * mm});
            skLineSegment(sketch, "E216.MirrorCS", {"start": v(5, -2) * mm, "end": v(8.5, -2) * mm});
            skLineSegment(sketch, "E217.MirrorCS", {"start": v(18.5, -2) * mm, "end": v(22, -2) * mm});
            skSolve(sketch);
        }
        {
            var Q0;
            Q0 = qSketchRegion(id + "F22", true);
            extrude(context, id + "F23", {"entities" : qUnion([Q0]), "operationType" : NewBodyOperationType.REMOVE, "oppositeDirection" : true, "depth" : 8 * mm, "offsetDistance" : 25 * mm});
        }
    });
